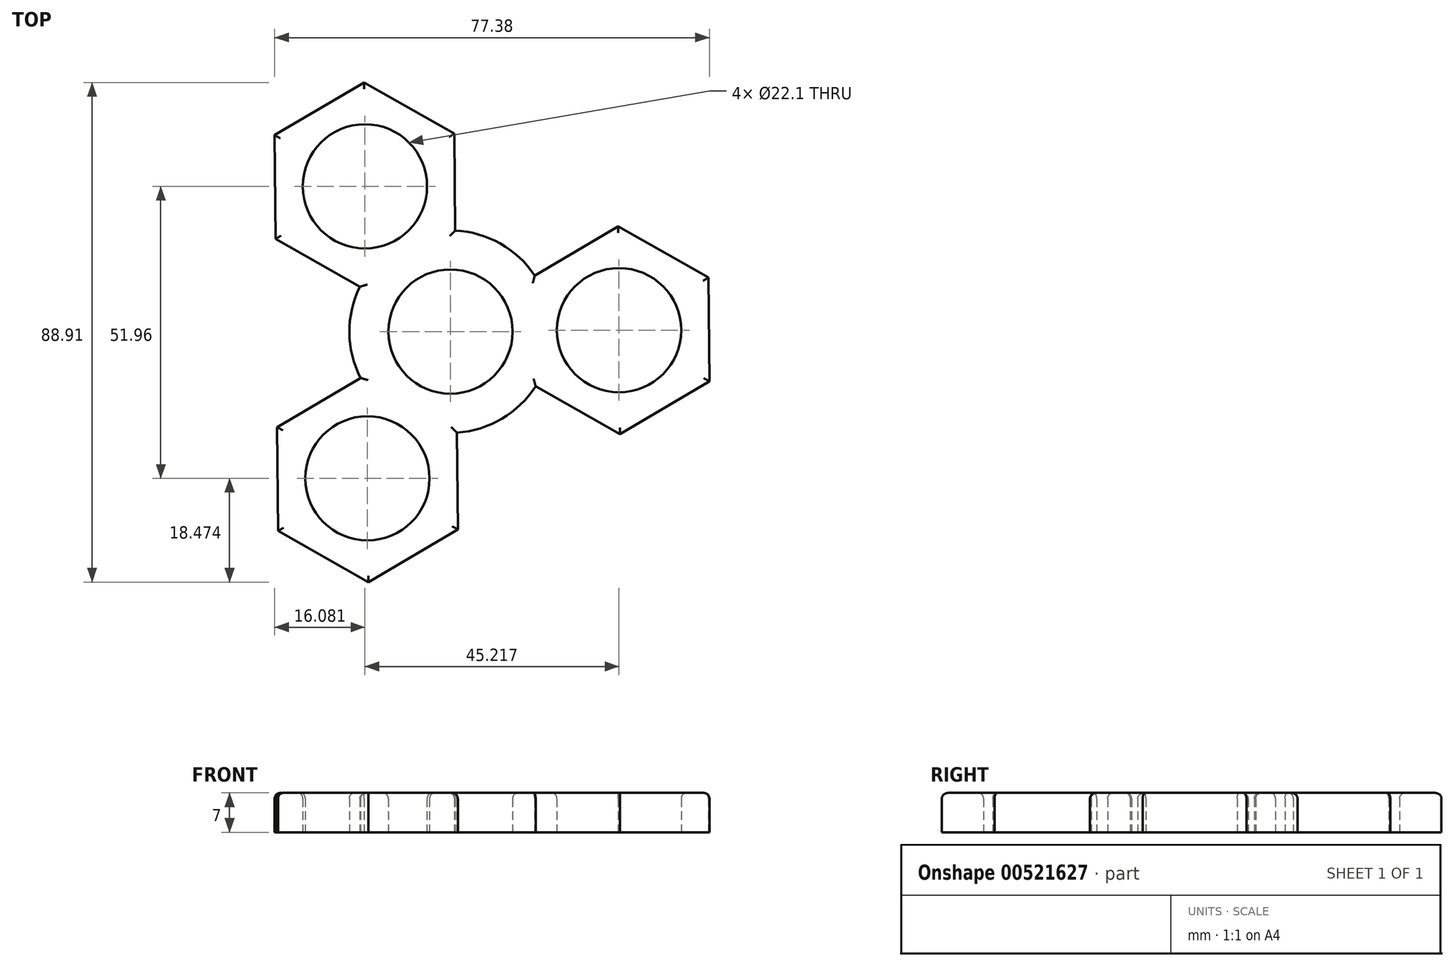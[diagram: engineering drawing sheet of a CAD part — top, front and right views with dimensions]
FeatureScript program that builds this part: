
annotation { "Feature Type Name" : "Feature", "Feature Type Description" : "" }
export const myFeature = defineFeature(function(context is Context, id is Id, definition is map)
    precondition{}
    {
        {
            var Q0;
            Q0=qCreatedBy(makeId("Top.planeOp"),FACE);
            var sketch = newSketch(context, id + "F0", { "sketchPlane" : qUnion([Q0])});
            skCircle(sketch, "E0", {"center": v(0, 0) * mm, "radius": 11.05 * mm});
            skCircle(sketch, "E1", {"center": v(0, 0) * mm, "radius": 18 * mm});
            skCircle(sketch, "E2", {"center": v(-15.22, 25.85) * mm, "radius": 11.05 * mm});
            skCircle(sketch, "E3", {"center": v(-14.78, -26.1) * mm, "radius": 11.05 * mm});
            skCircle(sketch, "E4", {"center": v(30, 0.25) * mm, "radius": 11.05 * mm});
            skCircle(sketch, "E5", {"center": v(-14.78, -26.1) * mm, "radius": 16 * mm});
            skCircle(sketch, "E6", {"center": v(-15.22, 25.85) * mm, "radius": 16 * mm});
            skCircle(sketch, "E7", {"center": v(30, 0.25) * mm, "radius": 16 * mm});
            skLineSegment(sketch, "E8", {"start": v(-15.22, 25.85) * mm, "end": v(0, 0) * mm});
            skLineSegment(sketch, "E9", {"start": v(30, 0.25) * mm, "end": v(0, 0) * mm});
            skLineSegment(sketch, "E10", {"start": v(-14.78, -26.1) * mm, "end": v(0, 0) * mm});
            skCircle(sketch, "E11.cCircle", {"center": v(-14.78, -26.1) * mm, "radius": 16 * mm, "construction": true});
            skLineSegment(sketch, "E11.0", {"start": v(-14.94, -7.63) * mm, "end": v(1.14, -16.73) * mm});
            skLineSegment(sketch, "E11.1", {"start": v(1.14, -16.73) * mm, "end": v(1.3, -35.2) * mm});
            skLineSegment(sketch, "E11.2", {"start": v(1.3, -35.2) * mm, "end": v(-14.62, -44.58) * mm});
            skLineSegment(sketch, "E11.3", {"start": v(-14.62, -44.58) * mm, "end": v(-30.7, -35.48) * mm});
            skLineSegment(sketch, "E11.4", {"start": v(-30.7, -35.48) * mm, "end": v(-30.86, -17) * mm});
            skLineSegment(sketch, "E11.5", {"start": v(-30.86, -17) * mm, "end": v(-14.94, -7.63) * mm});
            skPoint(sketch, "E11.0.midPoint", {"position": v(-6.9, -12.18) * mm});
            skCircle(sketch, "E12.cCircle", {"center": v(30, 0.25) * mm, "radius": 16 * mm, "construction": true});
            skLineSegment(sketch, "E12.0", {"start": v(14.08, -9.12) * mm, "end": v(13.92, 9.36) * mm});
            skLineSegment(sketch, "E12.1", {"start": v(13.92, 9.36) * mm, "end": v(29.84, 18.73) * mm});
            skLineSegment(sketch, "E12.2", {"start": v(29.84, 18.73) * mm, "end": v(45.92, 9.63) * mm});
            skLineSegment(sketch, "E12.3", {"start": v(45.92, 9.63) * mm, "end": v(46.08, -8.85) * mm});
            skLineSegment(sketch, "E12.4", {"start": v(46.08, -8.85) * mm, "end": v(30.15, -18.22) * mm});
            skLineSegment(sketch, "E12.5", {"start": v(30.15, -18.22) * mm, "end": v(14.08, -9.12) * mm});
            skPoint(sketch, "E12.0.midPoint", {"position": v(14, 0.12) * mm});
            skCircle(sketch, "E13.cCircle", {"center": v(-15.22, 25.85) * mm, "radius": 16 * mm, "construction": true});
            skLineSegment(sketch, "E13.0", {"start": v(0.86, 16.75) * mm, "end": v(-15.06, 7.38) * mm});
            skLineSegment(sketch, "E13.1", {"start": v(-15.06, 7.38) * mm, "end": v(-31.14, 16.48) * mm});
            skLineSegment(sketch, "E13.2", {"start": v(-31.14, 16.48) * mm, "end": v(-31.3, 34.96) * mm});
            skLineSegment(sketch, "E13.3", {"start": v(-31.3, 34.96) * mm, "end": v(-15.37, 44.33) * mm});
            skLineSegment(sketch, "E13.4", {"start": v(-15.37, 44.33) * mm, "end": v(0.7, 35.23) * mm});
            skLineSegment(sketch, "E13.5", {"start": v(0.7, 35.23) * mm, "end": v(0.86, 16.75) * mm});
            skPoint(sketch, "E13.0.midPoint", {"position": v(-7.1, 12.06) * mm});
            skSolve(sketch);
        }
        {
            var Q0;
            {var subQ0=sQuery(id+"F0.wireOp",EDGE,"e9zcL3uG-clMW-CB6R-mPn1-NTrwoYadkIhf");var subQ1=sQuery(id+"F0.wireOp",EDGE,"E0");var subQ2=makeQuery(id+"F0.imprint","INTERSECT",VERTEX,{"derivedFrom":[subQ1,subQ0]});Q0=makeQuery(id+"F0.imprint","IMPRINT",FACE,{"disambiguationData":[TD([[makeQuery(id+"F0.imprint","IMPRINT",EDGE,{"disambiguationData":[TD([[subQ2,-1.0]])],"derivedFrom":subQ1}),-1.0]])]});}
            var Q1;
            Q1=makeQuery(id+"F0.imprint","IMPRINT",FACE,{"disambiguationData":[TD([[makeQuery(id+"F0.imprint","IMPRINT",EDGE,{"derivedFrom":sQuery(id+"F0.wireOp",EDGE,"E3")}),-1.0]])]});
            var Q2;
            {var subQ0=sQuery(id+"F0.wireOp",EDGE,"fM1NJ59R-5Gtm-2Vz8-hERX-S4Y3RQeVmU9U");var subQ1=sQuery(id+"F0.wireOp",EDGE,"E1");var subQ2=makeQuery(id+"F0.imprint","INTERSECT",VERTEX,{"derivedFrom":[subQ1,subQ0]});Q2=makeQuery(id+"F0.imprint","IMPRINT",FACE,{"disambiguationData":[TD([[makeQuery(id+"F0.imprint","IMPRINT",EDGE,{"disambiguationData":[TD([[subQ2,-1.0]])],"derivedFrom":subQ1}),-1.0]])]});}
            var Q3;
            {var subQ0=sQuery(id+"F0.wireOp",EDGE,"oOAs71K8-LSWc-4CLp-Zzfn-c75iS4tNiohm");var subQ1=sQuery(id+"F0.wireOp",EDGE,"E0");var subQ2=makeQuery(id+"F0.imprint","INTERSECT",VERTEX,{"derivedFrom":[subQ1,subQ0]});Q3=makeQuery(id+"F0.imprint","IMPRINT",FACE,{"disambiguationData":[TD([[makeQuery(id+"F0.imprint","IMPRINT",EDGE,{"disambiguationData":[TD([[subQ2,1.0]])],"derivedFrom":subQ1}),-1.0]])]});}
            var Q4;
            {var subQ1=sQuery(id+"F0.wireOp",EDGE,"E1");var subQ3=sQuery(id+"F0.wireOp",EDGE,"jgwlEjWp-sw9u-VY17-f9nH-SewB5XZ8HkPX");var subQ4=makeQuery(id+"F0.imprint","INTERSECT",VERTEX,{"derivedFrom":[subQ1,subQ3]});Q4=makeQuery(id+"F0.imprint","IMPRINT",FACE,{"disambiguationData":[TD([[makeQuery(id+"F0.imprint","IMPRINT",EDGE,{"disambiguationData":[TD([[subQ4,1.0]])],"derivedFrom":subQ3}),1.0]])]});}
            var Q5;
            {var subQ0=sQuery(id+"F0.wireOp",EDGE,"e9zcL3uG-clMW-CB6R-mPn1-NTrwoYadkIhf");var subQ1=sQuery(id+"F0.wireOp",EDGE,"E0");var subQ2=makeQuery(id+"F0.imprint","INTERSECT",VERTEX,{"derivedFrom":[subQ1,subQ0]});Q5=makeQuery(id+"F0.imprint","IMPRINT",FACE,{"disambiguationData":[TD([[makeQuery(id+"F0.imprint","IMPRINT",EDGE,{"disambiguationData":[TD([[subQ2,1.0]])],"derivedFrom":subQ1}),-1.0]])]});}
            var Q6;
            {var subQ1=sQuery(id+"F0.wireOp",EDGE,"E1");var subQ3=sQuery(id+"F0.wireOp",EDGE,"oOAs71K8-LSWc-4CLp-Zzfn-c75iS4tNiohm");var subQ4=makeQuery(id+"F0.imprint","INTERSECT",VERTEX,{"derivedFrom":[subQ1,subQ3]});Q6=makeQuery(id+"F0.imprint","IMPRINT",FACE,{"disambiguationData":[TD([[makeQuery(id+"F0.imprint","IMPRINT",EDGE,{"disambiguationData":[TD([[subQ4,1.0]])],"derivedFrom":subQ3}),1.0]])]});}
            var Q7;
            Q7=makeQuery(id+"F0.imprint","IMPRINT",FACE,{"disambiguationData":[TD([[makeQuery(id+"F0.imprint","IMPRINT",EDGE,{"derivedFrom":sQuery(id+"F0.wireOp",EDGE,"E4")}),-1.0]])]});
            var Q8;
            Q8=makeQuery(id+"F0.imprint","IMPRINT",FACE,{"disambiguationData":[TD([[makeQuery(id+"F0.imprint","IMPRINT",EDGE,{"derivedFrom":sQuery(id+"F0.wireOp",EDGE,"E2")}),-1.0]])]});
            var Q9;
            {var subQ0=sQuery(id+"F0.wireOp",EDGE,"iWpcJYMW-lp7D-Rta9-vDUY-uTJnxPVIUKOB");var subQ1=sQuery(id+"F0.wireOp",EDGE,"E1");var subQ2=makeQuery(id+"F0.imprint","INTERSECT",VERTEX,{"derivedFrom":[subQ1,subQ0]});Q9=makeQuery(id+"F0.imprint","IMPRINT",FACE,{"disambiguationData":[TD([[makeQuery(id+"F0.imprint","IMPRINT",EDGE,{"disambiguationData":[TD([[subQ2,-1.0]])],"derivedFrom":subQ1}),-1.0]])]});}
            var Q10;
            {var subQ0=sQuery(id+"F0.wireOp",EDGE,"nEZrQKPM-t3Dd-AM5R-DWg6-JUV7cxrYPtug");var subQ1=sQuery(id+"F0.wireOp",EDGE,"E1");var subQ2=makeQuery(id+"F0.imprint","INTERSECT",VERTEX,{"derivedFrom":[subQ1,subQ0]});Q10=makeQuery(id+"F0.imprint","IMPRINT",FACE,{"disambiguationData":[TD([[makeQuery(id+"F0.imprint","IMPRINT",EDGE,{"disambiguationData":[TD([[subQ2,-1.0]])],"derivedFrom":subQ1}),-1.0]])]});}
            var Q11;
            {var subQ0=sQuery(id+"F0.wireOp",EDGE,"oOAs71K8-LSWc-4CLp-Zzfn-c75iS4tNiohm");var subQ1=sQuery(id+"F0.wireOp",EDGE,"E1");var subQ2=makeQuery(id+"F0.imprint","INTERSECT",VERTEX,{"derivedFrom":[subQ1,subQ0]});Q11=makeQuery(id+"F0.imprint","IMPRINT",FACE,{"disambiguationData":[TD([[makeQuery(id+"F0.imprint","IMPRINT",EDGE,{"disambiguationData":[TD([[subQ2,1.0]])],"derivedFrom":subQ1}),1.0]])]});}
            var Q12;
            {var subQ0=sQuery(id+"F0.wireOp",EDGE,"jgwlEjWp-sw9u-VY17-f9nH-SewB5XZ8HkPX");var subQ1=sQuery(id+"F0.wireOp",EDGE,"E1");var subQ2=makeQuery(id+"F0.imprint","INTERSECT",VERTEX,{"derivedFrom":[subQ1,subQ0]});Q12=makeQuery(id+"F0.imprint","IMPRINT",FACE,{"disambiguationData":[TD([[makeQuery(id+"F0.imprint","IMPRINT",EDGE,{"disambiguationData":[TD([[subQ2,1.0]])],"derivedFrom":subQ1}),1.0]])]});}
            var Q13;
            {var subQ1=sQuery(id+"F0.wireOp",EDGE,"E1");var subQ3=sQuery(id+"F0.wireOp",EDGE,"e9zcL3uG-clMW-CB6R-mPn1-NTrwoYadkIhf");var subQ4=makeQuery(id+"F0.imprint","INTERSECT",VERTEX,{"derivedFrom":[subQ1,subQ3]});Q13=makeQuery(id+"F0.imprint","IMPRINT",FACE,{"disambiguationData":[TD([[makeQuery(id+"F0.imprint","IMPRINT",EDGE,{"disambiguationData":[TD([[subQ4,1.0]])],"derivedFrom":subQ3}),1.0]])]});}
            var Q14;
            {var subQ0=sQuery(id+"F0.wireOp",EDGE,"e9zcL3uG-clMW-CB6R-mPn1-NTrwoYadkIhf");var subQ1=sQuery(id+"F0.wireOp",EDGE,"E1");var subQ2=makeQuery(id+"F0.imprint","INTERSECT",VERTEX,{"derivedFrom":[subQ1,subQ0]});Q14=makeQuery(id+"F0.imprint","IMPRINT",FACE,{"disambiguationData":[TD([[makeQuery(id+"F0.imprint","IMPRINT",EDGE,{"disambiguationData":[TD([[subQ2,1.0]])],"derivedFrom":subQ1}),1.0]])]});}
            var Q15;
            {var subQ0=sQuery(id+"F0.wireOp",EDGE,"E5");var subQ1=sQuery(id+"F0.wireOp",EDGE,"E1");var subQ2=makeQuery(id+"F0.imprint","INTERSECT",VERTEX,{"disambiguationData":[OD(0.0)],"derivedFrom":[subQ1,subQ0]});Q15=makeQuery(id+"F0.imprint","IMPRINT",FACE,{"disambiguationData":[TD([[makeQuery(id+"F0.imprint","IMPRINT",EDGE,{"disambiguationData":[TD([[subQ2,-1.0]])],"derivedFrom":subQ1}),1.0]])]});}
            var Q16;
            {var subQ0=sQuery(id+"F0.wireOp",EDGE,"E6");var subQ1=sQuery(id+"F0.wireOp",EDGE,"E1");var subQ2=makeQuery(id+"F0.imprint","INTERSECT",VERTEX,{"disambiguationData":[OD(0.0)],"derivedFrom":[subQ1,subQ0]});Q16=makeQuery(id+"F0.imprint","IMPRINT",FACE,{"disambiguationData":[TD([[makeQuery(id+"F0.imprint","IMPRINT",EDGE,{"disambiguationData":[TD([[subQ2,-1.0]])],"derivedFrom":subQ1}),1.0]])]});}
            var Q17;
            {var subQ0=sQuery(id+"F0.wireOp",EDGE,"E7");var subQ1=sQuery(id+"F0.wireOp",EDGE,"E1");var subQ2=makeQuery(id+"F0.imprint","INTERSECT",VERTEX,{"disambiguationData":[OD(0.0)],"derivedFrom":[subQ1,subQ0]});Q17=makeQuery(id+"F0.imprint","IMPRINT",FACE,{"disambiguationData":[TD([[makeQuery(id+"F0.imprint","IMPRINT",EDGE,{"disambiguationData":[TD([[subQ2,1.0]])],"derivedFrom":subQ1}),1.0]])]});}
            var Q18;
            {var subQ0=sQuery(id+"F0.wireOp",EDGE,"E13.1");var subQ1=sQuery(id+"F0.wireOp",EDGE,"E1");var subQ2=makeQuery(id+"F0.imprint","INTERSECT",VERTEX,{"derivedFrom":[subQ1,subQ0]});Q18=makeQuery(id+"F0.imprint","IMPRINT",FACE,{"disambiguationData":[TD([[makeQuery(id+"F0.imprint","IMPRINT",EDGE,{"disambiguationData":[TD([[subQ2,1.0]])],"derivedFrom":subQ1}),1.0]])]});}
            var Q19;
            {var subQ0=sQuery(id+"F0.wireOp",EDGE,"E13.5");var subQ1=sQuery(id+"F0.wireOp",EDGE,"E1");var subQ2=makeQuery(id+"F0.imprint","INTERSECT",VERTEX,{"derivedFrom":[subQ1,subQ0]});Q19=makeQuery(id+"F0.imprint","IMPRINT",FACE,{"disambiguationData":[TD([[makeQuery(id+"F0.imprint","IMPRINT",EDGE,{"disambiguationData":[TD([[subQ2,-1.0]])],"derivedFrom":subQ1}),1.0]])]});}
            var Q20;
            {var subQ0=sQuery(id+"F0.wireOp",EDGE,"E11.5");var subQ1=sQuery(id+"F0.wireOp",EDGE,"E1");var subQ2=makeQuery(id+"F0.imprint","INTERSECT",VERTEX,{"derivedFrom":[subQ1,subQ0]});Q20=makeQuery(id+"F0.imprint","IMPRINT",FACE,{"disambiguationData":[TD([[makeQuery(id+"F0.imprint","IMPRINT",EDGE,{"disambiguationData":[TD([[subQ2,-1.0]])],"derivedFrom":subQ1}),1.0]])]});}
            var Q21;
            {var subQ0=sQuery(id+"F0.wireOp",EDGE,"E11.1");var subQ1=sQuery(id+"F0.wireOp",EDGE,"E1");var subQ2=makeQuery(id+"F0.imprint","INTERSECT",VERTEX,{"derivedFrom":[subQ1,subQ0]});Q21=makeQuery(id+"F0.imprint","IMPRINT",FACE,{"disambiguationData":[TD([[makeQuery(id+"F0.imprint","IMPRINT",EDGE,{"disambiguationData":[TD([[subQ2,1.0]])],"derivedFrom":subQ1}),1.0]])]});}
            var Q22;
            {var subQ0=sQuery(id+"F0.wireOp",EDGE,"E12.2");var subQ1=sQuery(id+"F0.wireOp",EDGE,"E7");var subQ2=makeQuery(id+"F0.imprint","INTERSECT",VERTEX,{"derivedFrom":[subQ1,subQ0]});Q22=makeQuery(id+"F0.imprint","IMPRINT",FACE,{"disambiguationData":[TD([[makeQuery(id+"F0.imprint","IMPRINT",EDGE,{"disambiguationData":[TD([[subQ2,-1.0]])],"derivedFrom":subQ1}),-1.0]])]});}
            var Q23;
            {var subQ0=sQuery(id+"F0.wireOp",EDGE,"E12.2");var subQ1=sQuery(id+"F0.wireOp",EDGE,"E7");var subQ2=makeQuery(id+"F0.imprint","INTERSECT",VERTEX,{"derivedFrom":[subQ1,subQ0]});Q23=makeQuery(id+"F0.imprint","IMPRINT",FACE,{"disambiguationData":[TD([[makeQuery(id+"F0.imprint","IMPRINT",EDGE,{"disambiguationData":[TD([[subQ2,1.0]])],"derivedFrom":subQ1}),-1.0]])]});}
            var Q24;
            {var subQ0=sQuery(id+"F0.wireOp",EDGE,"E12.3");var subQ1=sQuery(id+"F0.wireOp",EDGE,"E7");var subQ2=makeQuery(id+"F0.imprint","INTERSECT",VERTEX,{"derivedFrom":[subQ1,subQ0]});Q24=makeQuery(id+"F0.imprint","IMPRINT",FACE,{"disambiguationData":[TD([[makeQuery(id+"F0.imprint","IMPRINT",EDGE,{"disambiguationData":[TD([[subQ2,1.0]])],"derivedFrom":subQ1}),-1.0]])]});}
            var Q25;
            {var subQ0=sQuery(id+"F0.wireOp",EDGE,"E12.5");var subQ1=sQuery(id+"F0.wireOp",EDGE,"E7");var subQ2=makeQuery(id+"F0.imprint","INTERSECT",VERTEX,{"derivedFrom":[subQ1,subQ0]});Q25=makeQuery(id+"F0.imprint","IMPRINT",FACE,{"disambiguationData":[TD([[makeQuery(id+"F0.imprint","IMPRINT",EDGE,{"disambiguationData":[TD([[subQ2,-1.0]])],"derivedFrom":subQ1}),-1.0]])]});}
            var Q26;
            {var subQ0=sQuery(id+"F0.wireOp",EDGE,"E11.1");var subQ1=sQuery(id+"F0.wireOp",EDGE,"E5");var subQ2=makeQuery(id+"F0.imprint","INTERSECT",VERTEX,{"derivedFrom":[subQ1,subQ0]});Q26=makeQuery(id+"F0.imprint","IMPRINT",FACE,{"disambiguationData":[TD([[makeQuery(id+"F0.imprint","IMPRINT",EDGE,{"disambiguationData":[TD([[subQ2,1.0]])],"derivedFrom":subQ1}),-1.0]])]});}
            var Q27;
            {var subQ0=sQuery(id+"F0.wireOp",EDGE,"E11.3");var subQ1=sQuery(id+"F0.wireOp",EDGE,"E5");var subQ2=makeQuery(id+"F0.imprint","INTERSECT",VERTEX,{"derivedFrom":[subQ1,subQ0]});Q27=makeQuery(id+"F0.imprint","IMPRINT",FACE,{"disambiguationData":[TD([[makeQuery(id+"F0.imprint","IMPRINT",EDGE,{"disambiguationData":[TD([[subQ2,-1.0]])],"derivedFrom":subQ1}),-1.0]])]});}
            var Q28;
            {var subQ0=sQuery(id+"F0.wireOp",EDGE,"E11.4");var subQ1=sQuery(id+"F0.wireOp",EDGE,"E5");var subQ2=makeQuery(id+"F0.imprint","INTERSECT",VERTEX,{"derivedFrom":[subQ1,subQ0]});Q28=makeQuery(id+"F0.imprint","IMPRINT",FACE,{"disambiguationData":[TD([[makeQuery(id+"F0.imprint","IMPRINT",EDGE,{"disambiguationData":[TD([[subQ2,-1.0]])],"derivedFrom":subQ1}),-1.0]])]});}
            var Q29;
            {var subQ0=sQuery(id+"F0.wireOp",EDGE,"E11.5");var subQ1=sQuery(id+"F0.wireOp",EDGE,"E5");var subQ2=makeQuery(id+"F0.imprint","INTERSECT",VERTEX,{"derivedFrom":[subQ1,subQ0]});Q29=makeQuery(id+"F0.imprint","IMPRINT",FACE,{"disambiguationData":[TD([[makeQuery(id+"F0.imprint","IMPRINT",EDGE,{"disambiguationData":[TD([[subQ2,-1.0]])],"derivedFrom":subQ1}),-1.0]])]});}
            var Q30;
            {var subQ0=sQuery(id+"F0.wireOp",EDGE,"E13.2");var subQ1=sQuery(id+"F0.wireOp",EDGE,"E6");var subQ2=makeQuery(id+"F0.imprint","INTERSECT",VERTEX,{"derivedFrom":[subQ1,subQ0]});Q30=makeQuery(id+"F0.imprint","IMPRINT",FACE,{"disambiguationData":[TD([[makeQuery(id+"F0.imprint","IMPRINT",EDGE,{"disambiguationData":[TD([[subQ2,-1.0]])],"derivedFrom":subQ1}),-1.0]])]});}
            var Q31;
            {var subQ0=sQuery(id+"F0.wireOp",EDGE,"E13.3");var subQ1=sQuery(id+"F0.wireOp",EDGE,"E6");var subQ2=makeQuery(id+"F0.imprint","INTERSECT",VERTEX,{"derivedFrom":[subQ1,subQ0]});Q31=makeQuery(id+"F0.imprint","IMPRINT",FACE,{"disambiguationData":[TD([[makeQuery(id+"F0.imprint","IMPRINT",EDGE,{"disambiguationData":[TD([[subQ2,-1.0]])],"derivedFrom":subQ1}),-1.0]])]});}
            var Q32;
            {var subQ0=sQuery(id+"F0.wireOp",EDGE,"E13.4");var subQ1=sQuery(id+"F0.wireOp",EDGE,"E6");var subQ2=makeQuery(id+"F0.imprint","INTERSECT",VERTEX,{"derivedFrom":[subQ1,subQ0]});Q32=makeQuery(id+"F0.imprint","IMPRINT",FACE,{"disambiguationData":[TD([[makeQuery(id+"F0.imprint","IMPRINT",EDGE,{"disambiguationData":[TD([[subQ2,-1.0]])],"derivedFrom":subQ1}),-1.0]])]});}
            var Q33;
            {var subQ0=sQuery(id+"F0.wireOp",EDGE,"E13.4");var subQ1=sQuery(id+"F0.wireOp",EDGE,"E6");var subQ2=makeQuery(id+"F0.imprint","INTERSECT",VERTEX,{"derivedFrom":[subQ1,subQ0]});Q33=makeQuery(id+"F0.imprint","IMPRINT",FACE,{"disambiguationData":[TD([[makeQuery(id+"F0.imprint","IMPRINT",EDGE,{"disambiguationData":[TD([[subQ2,1.0]])],"derivedFrom":subQ1}),-1.0]])]});}
            var Q34;
            {var subQ0=sQuery(id+"F0.wireOp",EDGE,"E12.1");var subQ1=sQuery(id+"F0.wireOp",EDGE,"E1");var subQ2=makeQuery(id+"F0.imprint","INTERSECT",VERTEX,{"derivedFrom":[subQ1,subQ0]});Q34=makeQuery(id+"F0.imprint","IMPRINT",FACE,{"disambiguationData":[TD([[makeQuery(id+"F0.imprint","IMPRINT",EDGE,{"disambiguationData":[TD([[subQ2,1.0]])],"derivedFrom":subQ1}),1.0]])]});}
            var Q35;
            {var subQ0=sQuery(id+"F0.wireOp",EDGE,"E12.5");var subQ1=sQuery(id+"F0.wireOp",EDGE,"E1");var subQ2=makeQuery(id+"F0.imprint","INTERSECT",VERTEX,{"derivedFrom":[subQ1,subQ0]});Q35=makeQuery(id+"F0.imprint","IMPRINT",FACE,{"disambiguationData":[TD([[makeQuery(id+"F0.imprint","IMPRINT",EDGE,{"disambiguationData":[TD([[subQ2,-1.0]])],"derivedFrom":subQ1}),1.0]])]});}
            extrude(context, id + "F1", {"entities" : qUnion([Q0, Q1, Q2, Q3, Q4, Q5, Q6, Q7, Q8, Q9, Q10, Q11, Q12, Q13, Q14, Q15, Q16, Q17, Q18, Q19, Q20, Q21, Q22, Q23, Q24, Q25, Q26, Q27, Q28, Q29, Q30, Q31, Q32, Q33, Q34, Q35]), "depth" : 7 * mm, "offsetDistance" : 25 * mm});
        }
        {
            var Q0;
            Q0=makeQuery(id+"F1.opExtrude","CAP_FACE",FACE,{"disambiguationData":[OSD([sQuery(id+"F0.wireOp",EDGE,"E0"),sQuery(id+"F0.wireOp",EDGE,"E2"),sQuery(id+"F0.wireOp",EDGE,"E3"),sQuery(id+"F0.wireOp",EDGE,"E4"),sQuery(id+"F0.wireOp",EDGE,"E5"),sQuery(id+"F0.wireOp",EDGE,"E6"),sQuery(id+"F0.wireOp",EDGE,"E7"),sQuery(id+"F0.wireOp",EDGE,"iWpcJYMW-lp7D-Rta9-vDUY-uTJnxPVIUKOB"),sQuery(id+"F0.wireOp",EDGE,"fM1NJ59R-5Gtm-2Vz8-hERX-S4Y3RQeVmU9U"),sQuery(id+"F0.wireOp",EDGE,"nEZrQKPM-t3Dd-AM5R-DWg6-JUV7cxrYPtug")])],"isStart":false});
            fillet(context, id + "F2", {"entities" : qUnion([Q0]), "radius" : 1 * mm, "tangentPropagation" : true, "allowEdgeOverflow" : false});
        }
    });
